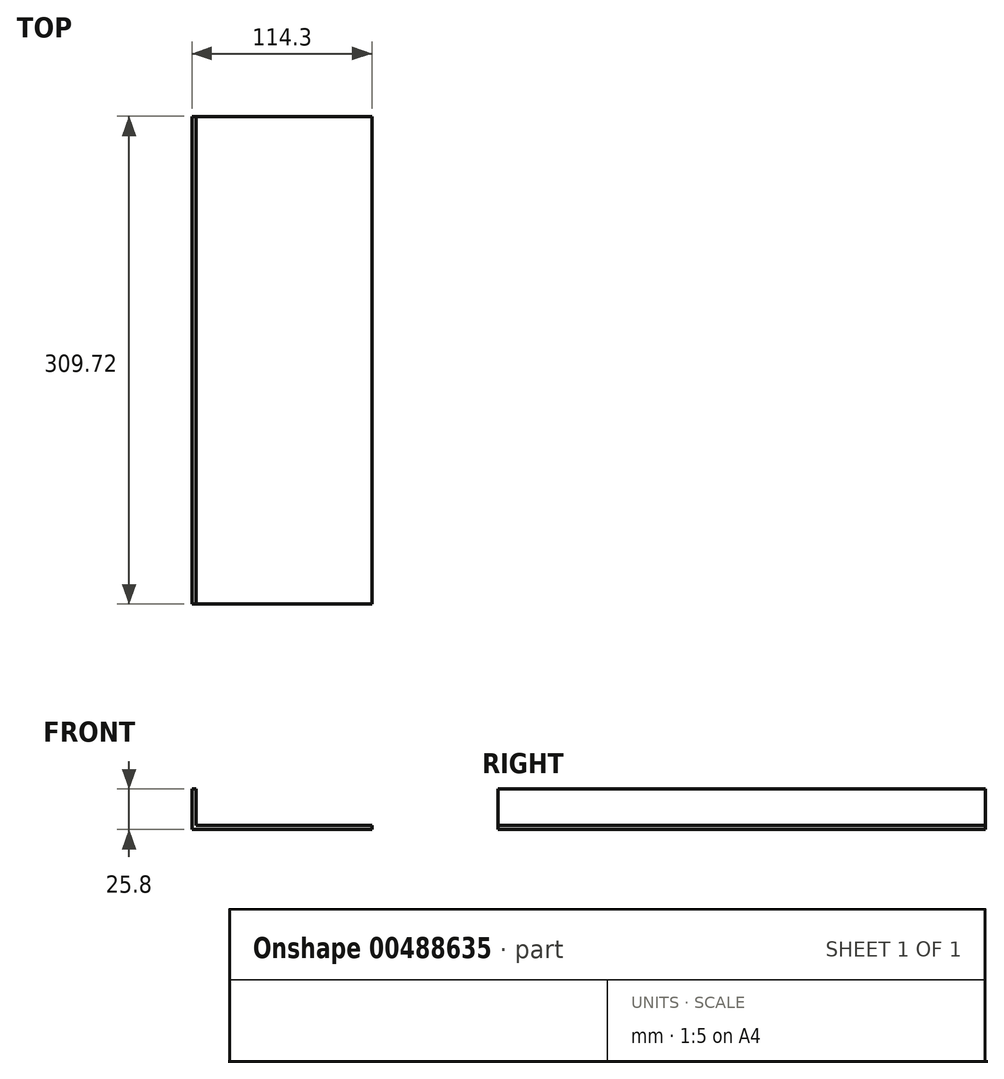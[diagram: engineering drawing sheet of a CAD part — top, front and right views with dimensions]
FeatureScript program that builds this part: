
annotation { "Feature Type Name" : "Feature", "Feature Type Description" : "" }
export const myFeature = defineFeature(function(context is Context, id is Id, definition is map)
    precondition{}
    {
        {
            var Q0;
            Q0=qCreatedBy(makeId("Right.planeOp"),FACE);
            var sketch = newSketch(context, id + "F0", { "sketchPlane" : qUnion([Q0])});
            skLineSegment(sketch, "E0.bottom", {"start": v(154.86, 12.9) * mm, "end": v(-154.86, 12.9) * mm});
            skLineSegment(sketch, "E0.top", {"start": v(154.86, -12.9) * mm, "end": v(-154.86, -12.9) * mm});
            skLineSegment(sketch, "E0.left", {"start": v(154.86, 12.9) * mm, "end": v(154.86, -12.9) * mm});
            skLineSegment(sketch, "E0.right", {"start": v(-154.86, 12.9) * mm, "end": v(-154.86, -12.9) * mm});
            skPoint(sketch, "E0.middle", {"position": v(0, 0) * mm});
            skSolve(sketch);
        }
        {
            var Q0;
            Q0=makeQuery(id+"F0.imprint","IMPRINT",FACE,{"disambiguationData":[TD([[makeQuery(id+"F0.imprint","IMPRINT",EDGE,{"derivedFrom":sQuery(id+"F0.wireOp",EDGE,"E0.bottom")}),1.0]])]});
            var Q1;
            Q1=sQuery(id+"F0.wireOp",EDGE,"E0.top");
            extrude(context, id + "F1", {"entities" : qUnion([Q0]), "surfaceEntities" : qUnion([Q1]), "depth" : 114.3 * mm});
        }
        {
            var Q0;
            Q0=makeQuery(id+"F1.opExtrude","SWEPT_FACE",FACE,{"disambiguationData":[OSD([sQuery(id+"F0.wireOp",EDGE,"E0.right")])]});
            var Q1;
            Q1=makeQuery(id+"F1.opExtrude","SWEPT_FACE",FACE,{"disambiguationData":[OSD([sQuery(id+"F0.wireOp",EDGE,"E0.bottom")])]});
            var Q2;
            Q2=makeQuery(id+"F1.opExtrude","CAP_FACE",FACE,{"disambiguationData":[OSD([sQuery(id+"F0.wireOp",EDGE,"E0.bottom"),sQuery(id+"F0.wireOp",EDGE,"E0.top"),sQuery(id+"F0.wireOp",EDGE,"E0.left"),sQuery(id+"F0.wireOp",EDGE,"E0.right")])],"isStart":false});
            var Q3;
            Q3=makeQuery(id+"F1.opExtrude","SWEPT_FACE",FACE,{"disambiguationData":[OSD([sQuery(id+"F0.wireOp",EDGE,"E0.left")])]});
            shell(context, id + "F2", {"entities" : qUnion([Q0, Q1, Q2, Q3]), "thickness" : 2.54 * mm});
        }
    });
